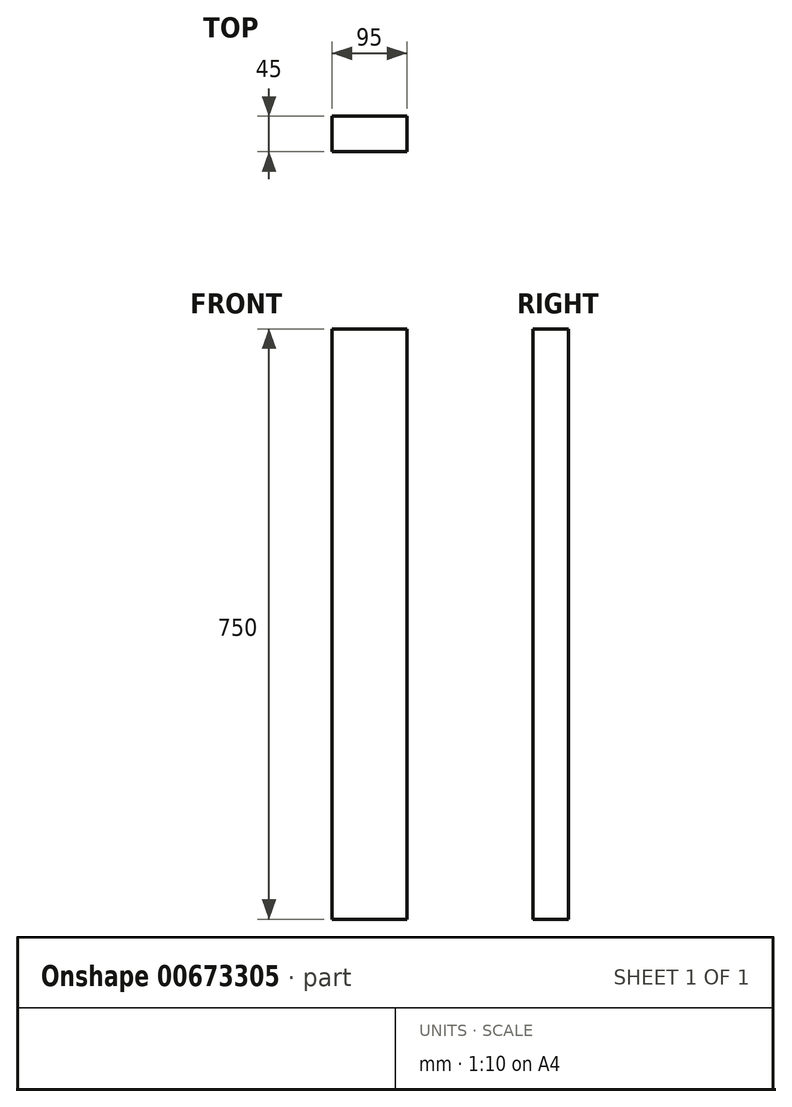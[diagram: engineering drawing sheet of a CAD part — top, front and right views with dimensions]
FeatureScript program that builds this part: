
annotation { "Feature Type Name" : "Feature", "Feature Type Description" : "" }
export const myFeature = defineFeature(function(context is Context, id is Id, definition is map)
    precondition{}
    {
        {
            var Q0;
            Q0=qCreatedBy(makeId("Top.planeOp"),FACE);
            var sketch = newSketch(context, id + "F0", { "sketchPlane" : qUnion([Q0])});
            skLineSegment(sketch, "E0.bottom", {"start": v(0, 0) * mm, "end": v(95, 0) * mm});
            skLineSegment(sketch, "E0.top", {"start": v(0, 45) * mm, "end": v(95, 45) * mm});
            skLineSegment(sketch, "E0.left", {"start": v(0, 0) * mm, "end": v(0, 45) * mm});
            skLineSegment(sketch, "E0.right", {"start": v(95, 0) * mm, "end": v(95, 45) * mm});
            skSolve(sketch);
        }
        {
            var Q0;
            Q0 = qSketchRegion(id + "F0", true);
            extrude(context, id + "F1", {"entities" : qUnion([Q0]), "depth" : 750 * mm, "offsetDistance" : 25 * mm});
        }
    });
